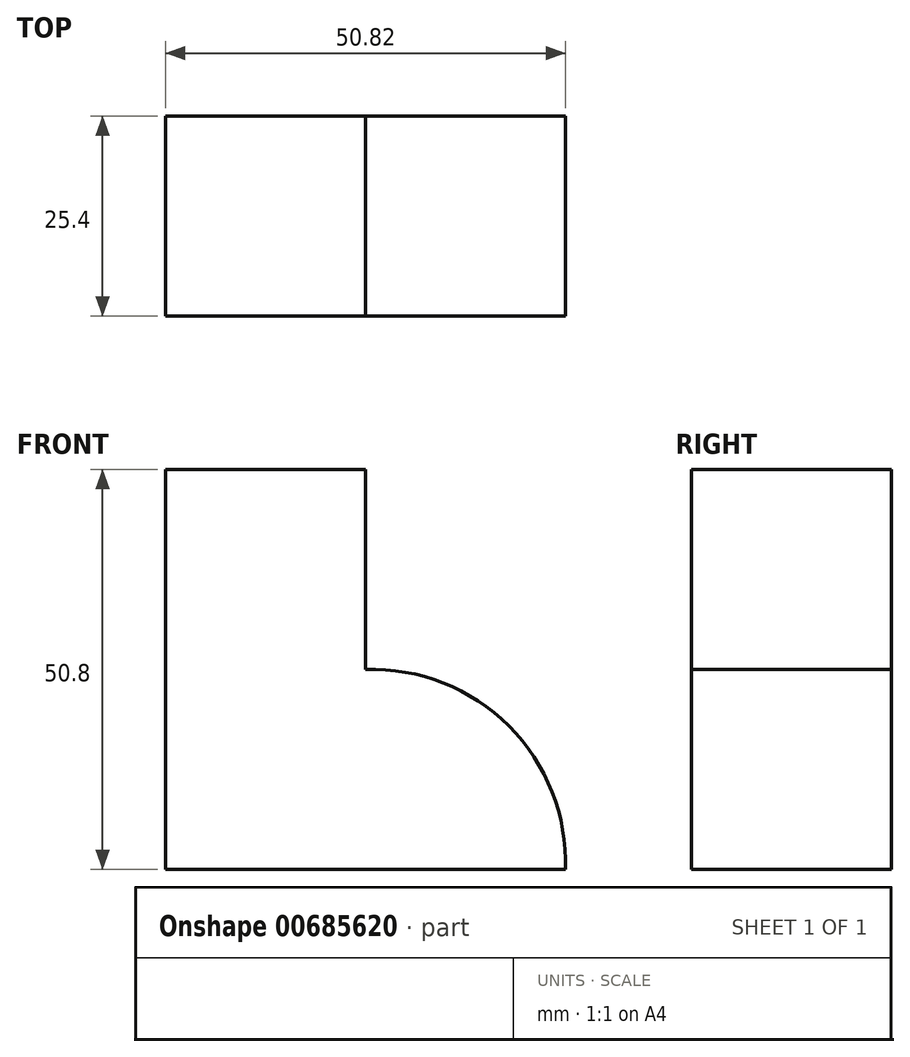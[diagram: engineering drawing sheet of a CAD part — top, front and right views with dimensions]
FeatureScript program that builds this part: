
annotation { "Feature Type Name" : "Feature", "Feature Type Description" : "" }
export const myFeature = defineFeature(function(context is Context, id is Id, definition is map)
    precondition{}
    {
        {
            var Q0;
            Q0=qCreatedBy(makeId("Front.planeOp"),FACE);
            var sketch = newSketch(context, id + "F0", { "sketchPlane" : qUnion([Q0])});
            skLineSegment(sketch, "E0", {"start": v(-61.33, 50.8) * mm, "end": v(-61.33, 0) * mm});
            skLineSegment(sketch, "E1", {"start": v(-61.33, 0) * mm, "end": v(-10.53, 0) * mm});
            skLineSegment(sketch, "E2", {"start": v(-61.33, 50.8) * mm, "end": v(-35.93, 50.8) * mm});
            skLineSegment(sketch, "E3", {"start": v(-35.93, 50.8) * mm, "end": v(-35.93, 25.4) * mm});
            skArc(sketch, "E4", {"start": v(-10.53, 0) * mm, "mid": v(-17.71, 18.22) * mm, "end": v(-35.93, 25.4) * mm});
            skSolve(sketch);
        }
        {
            var Q0;
            Q0 = qSketchRegion(id + "F0", true);
            extrude(context, id + "F1", {"entities" : qUnion([Q0]), "depth" : 25.4 * mm, "offsetDistance" : 25.4 * mm});
        }
    });
